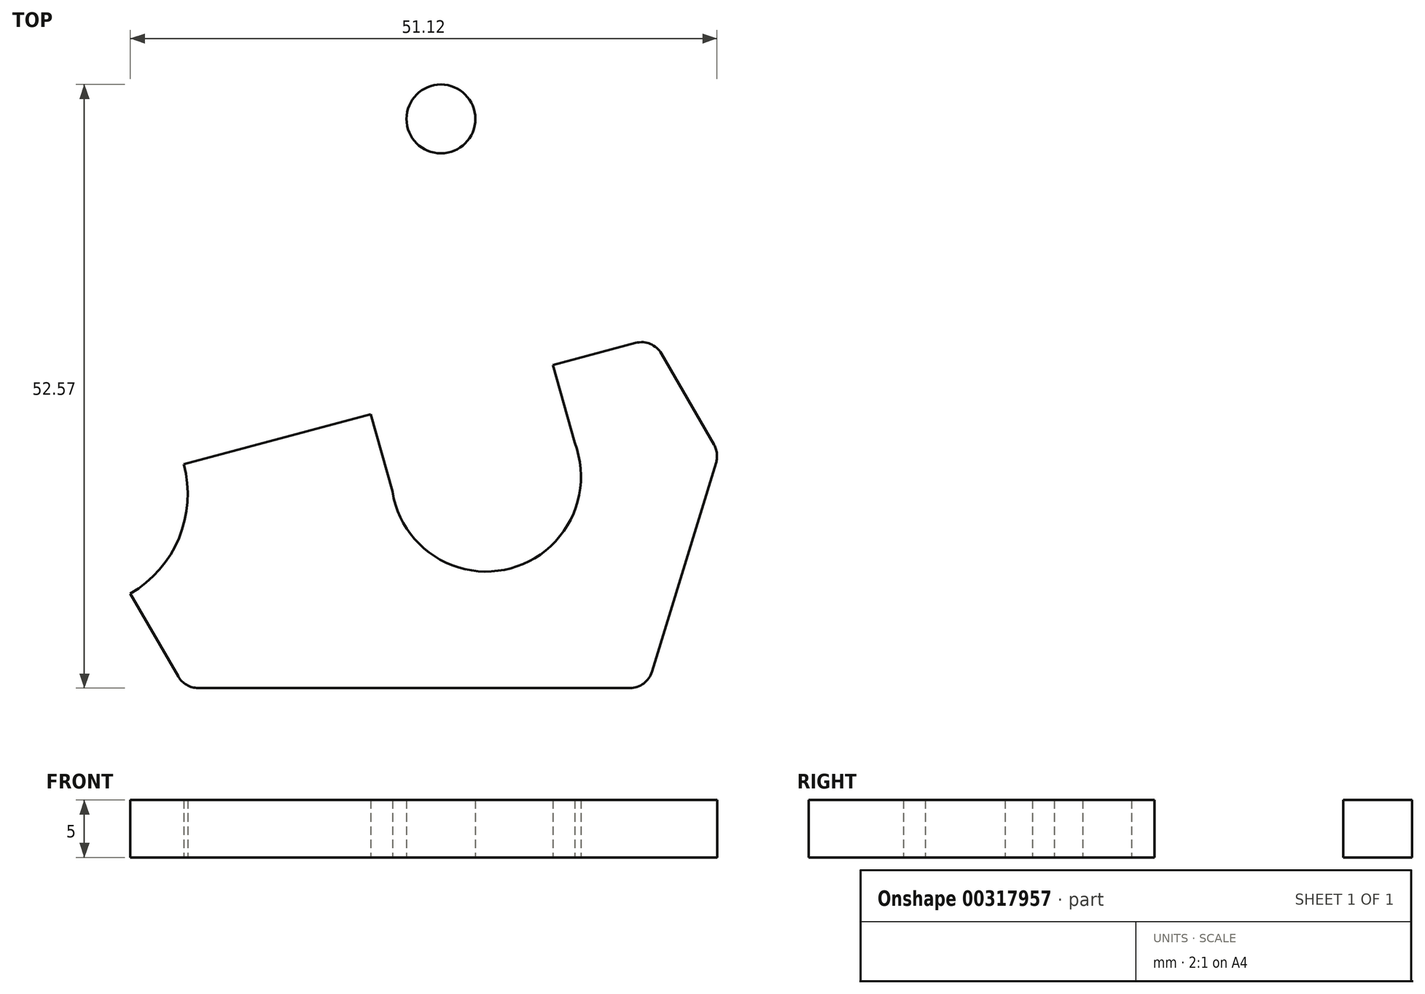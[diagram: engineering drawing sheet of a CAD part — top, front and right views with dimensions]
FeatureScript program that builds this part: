
annotation { "Feature Type Name" : "Feature", "Feature Type Description" : "" }
export const myFeature = defineFeature(function(context is Context, id is Id, definition is map)
    precondition{}
    {
        {
            var Q0;
            Q0=qCreatedBy(makeId("Top.planeOp"),FACE);
            var sketch = newSketch(context, id + "F0", { "sketchPlane" : qUnion([Q0])});
            skCircle(sketch, "E0", {"center": v(-33.32, 15.2) * mm, "radius": 3 * mm});
            skArc(sketch, "E1", {"start": v(55.9, 33.37) * mm, "mid": v(54.94, 34.21) * mm, "end": v(53.65, 34.3) * mm});
            skLineSegment(sketch, "E2", {"start": v(53.65, 34.3) * mm, "end": v(14.28, 23.73) * mm});
            skArc(sketch, "E3", {"start": v(14.28, 23.73) * mm, "mid": v(13.86, 17.3) * mm, "end": v(9.62, 12.47) * mm});
            skLineSegment(sketch, "E4", {"start": v(9.62, 12.47) * mm, "end": v(13.8, 5.25) * mm});
            skArc(sketch, "E5", {"start": v(13.8, 5.25) * mm, "mid": v(14.53, 4.52) * mm, "end": v(15.53, 4.25) * mm});
            skLineSegment(sketch, "E6", {"start": v(15.53, 4.25) * mm, "end": v(53.16, 4.25) * mm});
            skArc(sketch, "E7", {"start": v(53.16, 4.25) * mm, "mid": v(54.35, 4.64) * mm, "end": v(55.07, 5.66) * mm});
            skLineSegment(sketch, "E8", {"start": v(55.07, 5.66) * mm, "end": v(60.66, 23.85) * mm});
            skArc(sketch, "E9", {"start": v(60.66, 23.85) * mm, "mid": v(60.73, 24.66) * mm, "end": v(60.48, 25.44) * mm});
            skLineSegment(sketch, "E10", {"start": v(60.48, 25.44) * mm, "end": v(55.9, 33.37) * mm});
            skCircle(sketch, "E11", {"center": v(37.05, 15.2) * mm, "radius": 3 * mm});
            skLineSegment(sketch, "E12", {"start": v(45.04, -6.25) * mm, "end": v(46.93, -13) * mm});
            skArc(sketch, "E13", {"start": v(46.93, -13) * mm, "mid": v(41.36, -23.94) * mm, "end": v(31.04, -17.27) * mm});
            skLineSegment(sketch, "E14", {"start": v(31.04, -17.27) * mm, "end": v(29.15, -10.51) * mm});
            skLineSegment(sketch, "E15", {"start": v(29.15, -10.51) * mm, "end": v(12.87, -14.89) * mm});
            skArc(sketch, "E16", {"start": v(12.87, -14.89) * mm, "mid": v(12.45, -21.3) * mm, "end": v(8.2, -26.14) * mm});
            skLineSegment(sketch, "E17", {"start": v(8.2, -26.14) * mm, "end": v(12.38, -33.37) * mm});
            skArc(sketch, "E18", {"start": v(12.38, -33.37) * mm, "mid": v(13.11, -34.1) * mm, "end": v(14.11, -34.37) * mm});
            skLineSegment(sketch, "E19", {"start": v(14.11, -34.37) * mm, "end": v(51.75, -34.37) * mm});
            skArc(sketch, "E20", {"start": v(51.75, -34.37) * mm, "mid": v(52.94, -33.97) * mm, "end": v(53.66, -32.95) * mm});
            skLineSegment(sketch, "E21", {"start": v(53.66, -32.95) * mm, "end": v(59.25, -14.76) * mm});
            skArc(sketch, "E22", {"start": v(59.25, -14.76) * mm, "mid": v(59.32, -13.95) * mm, "end": v(59.07, -13.17) * mm});
            skLineSegment(sketch, "E23", {"start": v(59.07, -13.17) * mm, "end": v(54.49, -5.25) * mm});
            skArc(sketch, "E24", {"start": v(54.49, -5.25) * mm, "mid": v(53.52, -4.4) * mm, "end": v(52.24, -4.32) * mm});
            skLineSegment(sketch, "E25", {"start": v(52.24, -4.32) * mm, "end": v(45.04, -6.25) * mm});
            skLineSegment(sketch, "E26", {"start": v(-23.55, -6.25) * mm, "end": v(-21.67, -13) * mm});
            skArc(sketch, "E27", {"start": v(-21.67, -13) * mm, "mid": v(-27.23, -23.94) * mm, "end": v(-37.55, -17.27) * mm});
            skLineSegment(sketch, "E28", {"start": v(-37.55, -17.27) * mm, "end": v(-39.44, -10.51) * mm});
            skLineSegment(sketch, "E29", {"start": v(-39.44, -10.51) * mm, "end": v(-55.73, -14.89) * mm});
            skArc(sketch, "E30", {"start": v(-55.73, -14.89) * mm, "mid": v(-56.15, -21.3) * mm, "end": v(-60.38, -26.14) * mm});
            skLineSegment(sketch, "E31", {"start": v(-60.38, -26.14) * mm, "end": v(-56.21, -33.37) * mm});
            skArc(sketch, "E32", {"start": v(-56.21, -33.37) * mm, "mid": v(-55.48, -34.1) * mm, "end": v(-54.48, -34.37) * mm});
            skLineSegment(sketch, "E33", {"start": v(-54.48, -34.37) * mm, "end": v(-16.84, -34.37) * mm});
            skArc(sketch, "E34", {"start": v(-16.84, -34.37) * mm, "mid": v(-15.66, -33.97) * mm, "end": v(-14.93, -32.95) * mm});
            skLineSegment(sketch, "E35", {"start": v(-14.93, -32.95) * mm, "end": v(-9.35, -14.76) * mm});
            skArc(sketch, "E36", {"start": v(-9.35, -14.76) * mm, "mid": v(-9.27, -13.95) * mm, "end": v(-9.53, -13.17) * mm});
            skLineSegment(sketch, "E37", {"start": v(-9.53, -13.17) * mm, "end": v(-14.1, -5.25) * mm});
            skArc(sketch, "E38", {"start": v(-14.1, -5.25) * mm, "mid": v(-15.07, -4.4) * mm, "end": v(-16.35, -4.32) * mm});
            skLineSegment(sketch, "E39", {"start": v(-16.35, -4.32) * mm, "end": v(-23.55, -6.25) * mm});
            skArc(sketch, "E40", {"start": v(-14.47, 33.37) * mm, "mid": v(-15.43, 34.21) * mm, "end": v(-16.72, 34.3) * mm});
            skLineSegment(sketch, "E41", {"start": v(-16.72, 34.3) * mm, "end": v(-56.09, 23.73) * mm});
            skArc(sketch, "E42", {"start": v(-56.09, 23.73) * mm, "mid": v(-56.5, 17.3) * mm, "end": v(-60.75, 12.47) * mm});
            skLineSegment(sketch, "E43", {"start": v(-60.75, 12.47) * mm, "end": v(-56.57, 5.25) * mm});
            skArc(sketch, "E44", {"start": v(-56.57, 5.25) * mm, "mid": v(-55.84, 4.52) * mm, "end": v(-54.84, 4.25) * mm});
            skLineSegment(sketch, "E45", {"start": v(-54.84, 4.25) * mm, "end": v(-17.2, 4.25) * mm});
            skArc(sketch, "E46", {"start": v(-17.2, 4.25) * mm, "mid": v(-16.02, 4.64) * mm, "end": v(-15.3, 5.66) * mm});
            skLineSegment(sketch, "E47", {"start": v(-15.3, 5.66) * mm, "end": v(-9.7, 23.85) * mm});
            skArc(sketch, "E48", {"start": v(-9.7, 23.85) * mm, "mid": v(-9.63, 24.66) * mm, "end": v(-9.89, 25.44) * mm});
            skLineSegment(sketch, "E49", {"start": v(-9.89, 25.44) * mm, "end": v(-14.47, 33.37) * mm});
            skSolve(sketch);
        }
        {
            var Q0;
            Q0=makeQuery(id+"F0.imprint","IMPRINT",FACE,{"disambiguationData":[TD([[makeQuery(id+"F0.imprint","IMPRINT",EDGE,{"derivedFrom":sQuery(id+"F0.wireOp",EDGE,"E0")}),1.0]])]});
            extrude(context, id + "F1", {"entities" : qUnion([Q0]), "depth" : 5 * mm});
        }
        {
            var Q0;
            Q0=makeQuery(id+"F0.imprint","IMPRINT",FACE,{"disambiguationData":[TD([[makeQuery(id+"F0.imprint","IMPRINT",EDGE,{"derivedFrom":sQuery(id+"F0.wireOp",EDGE,"E26")}),1.0]])]});
            extrude(context, id + "F2", {"entities" : qUnion([Q0]), "depth" : 5 * mm});
        }
    });
